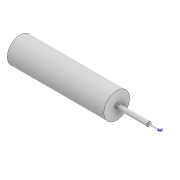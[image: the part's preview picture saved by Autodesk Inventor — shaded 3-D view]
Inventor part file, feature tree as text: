
AUTODESK INVENTOR PART (.ipt)
format: ipt  version: 2021 (Build 250183000, 183)  size: 121,856 bytes
history: native  units: mm
features: sketch x10, extrude x8, chamfer x1
ambient origin geometry x8: Origin, YZ Plane, XZ Plane, XY Plane, X Axis, Y Axis, Z Axis, Center Point
bodies: Solid1 (feature_tree)
feature tree (19):
  extrude  "Extrusion1"  Depth=150.0mm TaperAngle=0.0deg
  extrude  "Extrusion2"  Depth=140.0mm TaperAngle=0.0deg
  extrude  "Extrusion3"  Depth=1.0mm TaperAngle=0.0deg
  extrude  "Extrusion4"  Depth=10.0mm TaperAngle=0.0deg
  sketch  "Sketch5"  dims[d13=4.9mm d14=4.9mm]
  extrude  "Extrusion5"  Depth=4.9mm
  extrude  "Extrusion6"  Depth=50.0mm TaperAngle=0.0deg
  sketch  "Sketch7"  dims[d19=4.8mm d20=4.5mm d21=140.0mm d22=0.0mm]
  sketch  "Sketch8"  dims[d23=1.0mm d24=2.0mm d25=45.0deg d28=120.0mm]
  sketch  "Sketch9"  dims[d29=450.0mm d30=0.0mm]
  extrude  "Extrusion7"  Depth=140.0mm
  chamfer  "Chamfer1"  Distance=140.0mm
  extrude  "Extrusion8"  Depth=1.0mm
  sketch  "Sketch1"  dims[d0=20.0mm d1=150.0mm d2=0.0mm]
  sketch  "Sketch2"  dims[d4=19.0mm d5=140.0mm d6=0.0mm]
  sketch  "Sketch3"  dims[d7=5.0mm d8=1.0mm d9=0.0mm]
  sketch  "Sketch4"  dims[d10=5.0mm d11=10.0mm d12=0.0mm]
  sketch  "Sketch6"  dims[d15=120.0mm d16=0.0mm d17=50.0mm d18=0.0mm]
  sketch  "Sketch10"  dims[d31=0.5mm d32=0.872665mm d33=0.5mm d34=0.872665mm]
